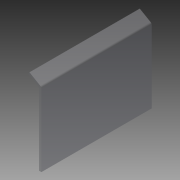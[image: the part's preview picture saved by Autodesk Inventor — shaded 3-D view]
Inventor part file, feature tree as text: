
AUTODESK INVENTOR PART (.ipt)
format: ipt  version: 2013 (Build 170138000, 138)  size: 78,848 bytes
history: native  units: in
note: dims shown in document units (in); Inventor stores cm internally (conversion verified against a paired STEP export)
features: extrude x1, sketch x1
ambient origin geometry x8: Origin, YZ Plane, XZ Plane, XY Plane, X Axis, Y Axis, Z Axis, Center Point
bodies: Solid1 (feature_tree)
feature tree (2):
  extrude  "Extrusion1"  Depth=0.25in
  sketch  "Sketch1"  dims[d0=0.25in d1=0.25in d2=120.0deg d3=1.5in d4=8.0in d6=0.25in d7=12.0in d8=0.0in]
